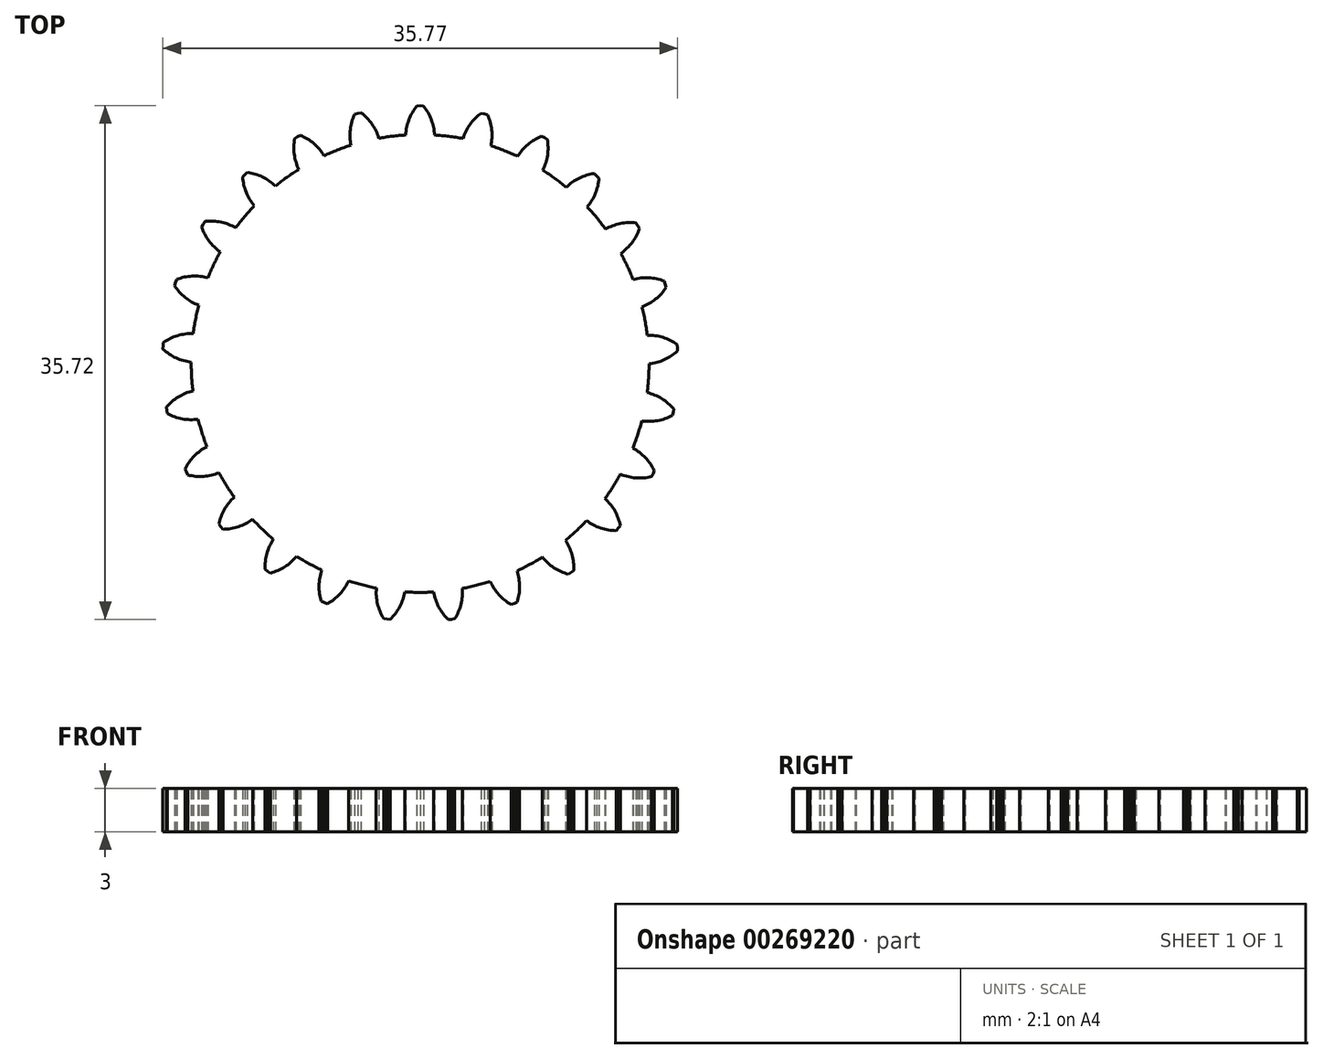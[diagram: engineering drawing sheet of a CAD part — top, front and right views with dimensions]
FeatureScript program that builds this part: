
annotation { "Feature Type Name" : "Feature", "Feature Type Description" : "" }
export const myFeature = defineFeature(function(context is Context, id is Id, definition is map)
    precondition{}
    {
        {
            var Q0;
            Q0=qCreatedBy(makeId("Top.planeOp"),FACE);
            var sketch = newSketch(context, id + "F0", { "sketchPlane" : qUnion([Q0])});
            skCircle(sketch, "E0", {"center": v(0, 0) * mm, "radius": 15.91 * mm});
            skCircle(sketch, "E1", {"center": v(0, 0) * mm, "radius": 16.91 * mm, "construction": true});
            skCircle(sketch, "E2", {"center": v(0, 0) * mm, "radius": 17.91 * mm, "construction": true});
            skLineSegment(sketch, "E3", {"start": v(0, 0) * mm, "end": v(0, 30.14) * mm, "construction": true});
            skLineSegment(sketch, "E4", {"start": v(0, 0) * mm, "end": v(-1.77, 28.18) * mm, "construction": true});
            skPoint(sketch, "E5", {"position": v(-1, 15.88) * mm});
            skPoint(sketch, "E6", {"position": v(0, 15.91) * mm});
            skLineSegment(sketch, "E7", {"start": v(-1, 15.88) * mm, "end": v(0, 15.91) * mm, "construction": true});
            skCircle(sketch, "E8", {"center": v(0, 16.91) * mm, "radius": 2.73 * mm, "construction": true});
            skLineSegment(sketch, "E9", {"start": v(0, 17.92) * mm, "end": v(0, 15.91) * mm});
            skArc(sketch, "E10", {"start": v(-0.23, 17.9) * mm, "mid": v(-0.78, 16.96) * mm, "end": v(-1, 15.88) * mm});
            skArc(sketch, "E11", {"start": v(-1, 15.88) * mm, "mid": v(5.7, 14.49) * mm, "end": v(-0.23, 17.9) * mm, "construction": true});
            skLineSegment(sketch, "E12", {"start": v(-0.23, 17.9) * mm, "end": v(0, 17.92) * mm});
            skLineSegment(sketch, "E13.MirrorCS", {"start": v(0.23, 17.9) * mm, "end": v(0, 17.92) * mm});
            skArc(sketch, "E14.MirrorCS", {"start": v(0.23, 17.9) * mm, "mid": v(0.78, 16.96) * mm, "end": v(1, 15.88) * mm});
            skLineSegment(sketch, "E15.1.0", {"start": v(4.46, 17.35) * mm, "end": v(3.96, 15.41) * mm});
            skPoint(sketch, "E15.1.1", {"position": v(3.96, 15.41) * mm});
            skArc(sketch, "E15.1.2", {"start": v(4.68, 17.28) * mm, "mid": v(4.97, 16.23) * mm, "end": v(4.92, 15.13) * mm});
            skPoint(sketch, "E15.1.3", {"position": v(2.99, 15.63) * mm});
            skLineSegment(sketch, "E15.1.4", {"start": v(2.99, 15.63) * mm, "end": v(3.96, 15.41) * mm, "construction": true});
            skArc(sketch, "E15.1.5", {"start": v(4.24, 17.4) * mm, "mid": v(3.47, 16.61) * mm, "end": v(2.99, 15.63) * mm});
            skLineSegment(sketch, "E15.1.6", {"start": v(4.68, 17.28) * mm, "end": v(4.46, 17.35) * mm});
            skLineSegment(sketch, "E15.1.7", {"start": v(4.24, 17.4) * mm, "end": v(4.46, 17.35) * mm});
            skLineSegment(sketch, "E15.2.0", {"start": v(8.64, 15.7) * mm, "end": v(7.67, 13.94) * mm});
            skPoint(sketch, "E15.2.1", {"position": v(7.67, 13.94) * mm});
            skArc(sketch, "E15.2.2", {"start": v(8.84, 15.58) * mm, "mid": v(8.86, 14.48) * mm, "end": v(8.53, 13.43) * mm});
            skPoint(sketch, "E15.2.3", {"position": v(6.78, 14.4) * mm});
            skLineSegment(sketch, "E15.2.4", {"start": v(6.78, 14.4) * mm, "end": v(7.67, 13.94) * mm, "construction": true});
            skArc(sketch, "E15.2.5", {"start": v(8.43, 15.8) * mm, "mid": v(7.5, 15.23) * mm, "end": v(6.78, 14.4) * mm});
            skLineSegment(sketch, "E15.2.6", {"start": v(8.84, 15.58) * mm, "end": v(8.64, 15.7) * mm});
            skLineSegment(sketch, "E15.2.7", {"start": v(8.43, 15.8) * mm, "end": v(8.64, 15.7) * mm});
            skLineSegment(sketch, "E15.3.0", {"start": v(12.28, 13.05) * mm, "end": v(10.9, 11.6) * mm});
            skPoint(sketch, "E15.3.1", {"position": v(10.9, 11.6) * mm});
            skArc(sketch, "E15.3.2", {"start": v(12.43, 12.88) * mm, "mid": v(12.18, 11.82) * mm, "end": v(11.61, 10.88) * mm});
            skPoint(sketch, "E15.3.3", {"position": v(10.15, 12.25) * mm});
            skLineSegment(sketch, "E15.3.4", {"start": v(10.15, 12.25) * mm, "end": v(10.9, 11.6) * mm, "construction": true});
            skArc(sketch, "E15.3.5", {"start": v(12.1, 13.2) * mm, "mid": v(11.05, 12.88) * mm, "end": v(10.15, 12.25) * mm});
            skLineSegment(sketch, "E15.3.6", {"start": v(12.43, 12.88) * mm, "end": v(12.28, 13.05) * mm});
            skLineSegment(sketch, "E15.3.7", {"start": v(12.1, 13.2) * mm, "end": v(12.28, 13.05) * mm});
            skLineSegment(sketch, "E15.4.0", {"start": v(15.14, 9.58) * mm, "end": v(13.45, 8.51) * mm});
            skPoint(sketch, "E15.4.1", {"position": v(13.45, 8.51) * mm});
            skArc(sketch, "E15.4.2", {"start": v(15.25, 9.38) * mm, "mid": v(14.74, 8.41) * mm, "end": v(13.95, 7.65) * mm});
            skPoint(sketch, "E15.4.3", {"position": v(12.88, 9.34) * mm});
            skLineSegment(sketch, "E15.4.4", {"start": v(12.88, 9.34) * mm, "end": v(13.45, 8.51) * mm, "construction": true});
            skArc(sketch, "E15.4.5", {"start": v(15, 9.77) * mm, "mid": v(13.91, 9.72) * mm, "end": v(12.88, 9.34) * mm});
            skLineSegment(sketch, "E15.4.6", {"start": v(15.25, 9.38) * mm, "end": v(15.14, 9.58) * mm});
            skLineSegment(sketch, "E15.4.7", {"start": v(15, 9.77) * mm, "end": v(15.14, 9.58) * mm});
            skLineSegment(sketch, "E15.5.0", {"start": v(17.05, 5.51) * mm, "end": v(15.14, 4.9) * mm});
            skPoint(sketch, "E15.5.1", {"position": v(15.14, 4.9) * mm});
            skArc(sketch, "E15.5.2", {"start": v(17.1, 5.3) * mm, "mid": v(16.37, 4.48) * mm, "end": v(15.42, 3.93) * mm});
            skPoint(sketch, "E15.5.3", {"position": v(14.8, 5.84) * mm});
            skLineSegment(sketch, "E15.5.4", {"start": v(14.8, 5.84) * mm, "end": v(15.14, 4.9) * mm, "construction": true});
            skArc(sketch, "E15.5.5", {"start": v(16.97, 5.73) * mm, "mid": v(15.9, 5.95) * mm, "end": v(14.8, 5.84) * mm});
            skLineSegment(sketch, "E15.5.6", {"start": v(17.1, 5.3) * mm, "end": v(17.05, 5.51) * mm});
            skLineSegment(sketch, "E15.5.7", {"start": v(16.97, 5.73) * mm, "end": v(17.05, 5.51) * mm});
            skLineSegment(sketch, "E15.6.0", {"start": v(17.88, 1.1) * mm, "end": v(15.88, 0.97) * mm});
            skPoint(sketch, "E15.6.1", {"position": v(15.88, 0.97) * mm});
            skArc(sketch, "E15.6.2", {"start": v(17.89, 0.86) * mm, "mid": v(16.97, 0.26) * mm, "end": v(15.91, -0.03) * mm});
            skPoint(sketch, "E15.6.3", {"position": v(15.8, 1.97) * mm});
            skLineSegment(sketch, "E15.6.4", {"start": v(15.8, 1.97) * mm, "end": v(15.88, 0.97) * mm, "construction": true});
            skArc(sketch, "E15.6.5", {"start": v(17.86, 1.32) * mm, "mid": v(16.88, 1.8) * mm, "end": v(15.8, 1.97) * mm});
            skLineSegment(sketch, "E15.6.6", {"start": v(17.89, 0.86) * mm, "end": v(17.88, 1.1) * mm});
            skLineSegment(sketch, "E15.6.7", {"start": v(17.86, 1.32) * mm, "end": v(17.88, 1.1) * mm});
            skLineSegment(sketch, "E15.7.0", {"start": v(17.6, -3.4) * mm, "end": v(15.63, -3.01) * mm});
            skPoint(sketch, "E15.7.1", {"position": v(15.63, -3.01) * mm});
            skArc(sketch, "E15.7.2", {"start": v(17.54, -3.62) * mm, "mid": v(16.5, -3.97) * mm, "end": v(15.4, -3.99) * mm});
            skPoint(sketch, "E15.7.3", {"position": v(15.78, -2.03) * mm});
            skLineSegment(sketch, "E15.7.4", {"start": v(15.78, -2.03) * mm, "end": v(15.63, -3.01) * mm, "construction": true});
            skArc(sketch, "E15.7.5", {"start": v(17.62, -3.17) * mm, "mid": v(16.8, -2.45) * mm, "end": v(15.78, -2.03) * mm});
            skLineSegment(sketch, "E15.7.6", {"start": v(17.54, -3.62) * mm, "end": v(17.6, -3.4) * mm});
            skLineSegment(sketch, "E15.7.7", {"start": v(17.62, -3.17) * mm, "end": v(17.6, -3.4) * mm});
            skLineSegment(sketch, "E15.8.0", {"start": v(16.2, -7.67) * mm, "end": v(14.38, -6.8) * mm});
            skPoint(sketch, "E15.8.1", {"position": v(14.38, -6.8) * mm});
            skArc(sketch, "E15.8.2", {"start": v(16.09, -7.87) * mm, "mid": v(15, -7.96) * mm, "end": v(13.93, -7.7) * mm});
            skPoint(sketch, "E15.8.3", {"position": v(14.78, -5.9) * mm});
            skLineSegment(sketch, "E15.8.4", {"start": v(14.78, -5.9) * mm, "end": v(14.38, -6.8) * mm, "construction": true});
            skArc(sketch, "E15.8.5", {"start": v(16.28, -7.45) * mm, "mid": v(15.66, -6.55) * mm, "end": v(14.78, -5.9) * mm});
            skLineSegment(sketch, "E15.8.6", {"start": v(16.09, -7.87) * mm, "end": v(16.2, -7.67) * mm});
            skLineSegment(sketch, "E15.8.7", {"start": v(16.28, -7.45) * mm, "end": v(16.2, -7.67) * mm});
            skLineSegment(sketch, "E15.9.0", {"start": v(13.77, -11.46) * mm, "end": v(12.23, -10.18) * mm});
            skPoint(sketch, "E15.9.1", {"position": v(12.23, -10.18) * mm});
            skArc(sketch, "E15.9.2", {"start": v(13.62, -11.63) * mm, "mid": v(12.54, -11.44) * mm, "end": v(11.57, -10.92) * mm});
            skPoint(sketch, "E15.9.3", {"position": v(12.85, -9.39) * mm});
            skLineSegment(sketch, "E15.9.4", {"start": v(12.85, -9.39) * mm, "end": v(12.23, -10.18) * mm, "construction": true});
            skArc(sketch, "E15.9.5", {"start": v(13.91, -11.27) * mm, "mid": v(13.53, -10.25) * mm, "end": v(12.85, -9.39) * mm});
            skLineSegment(sketch, "E15.9.6", {"start": v(13.62, -11.63) * mm, "end": v(13.77, -11.46) * mm});
            skLineSegment(sketch, "E15.9.7", {"start": v(13.91, -11.27) * mm, "end": v(13.77, -11.46) * mm});
            skLineSegment(sketch, "E15.10.0", {"start": v(10.49, -14.52) * mm, "end": v(9.32, -12.9) * mm});
            skPoint(sketch, "E15.10.1", {"position": v(9.32, -12.9) * mm});
            skArc(sketch, "E15.10.2", {"start": v(10.3, -14.65) * mm, "mid": v(9.3, -14.2) * mm, "end": v(8.49, -13.46) * mm});
            skPoint(sketch, "E15.10.3", {"position": v(10.1, -12.3) * mm});
            skLineSegment(sketch, "E15.10.4", {"start": v(10.1, -12.3) * mm, "end": v(9.32, -12.9) * mm, "construction": true});
            skArc(sketch, "E15.10.5", {"start": v(10.67, -14.38) * mm, "mid": v(10.56, -13.3) * mm, "end": v(10.1, -12.3) * mm});
            skLineSegment(sketch, "E15.10.6", {"start": v(10.3, -14.65) * mm, "end": v(10.49, -14.52) * mm});
            skLineSegment(sketch, "E15.10.7", {"start": v(10.67, -14.38) * mm, "end": v(10.49, -14.52) * mm});
            skLineSegment(sketch, "E15.11.0", {"start": v(6.54, -16.68) * mm, "end": v(5.81, -14.81) * mm});
            skPoint(sketch, "E15.11.1", {"position": v(5.81, -14.81) * mm});
            skArc(sketch, "E15.11.2", {"start": v(6.33, -16.75) * mm, "mid": v(5.47, -16.07) * mm, "end": v(4.87, -15.15) * mm});
            skPoint(sketch, "E15.11.3", {"position": v(6.73, -14.42) * mm});
            skLineSegment(sketch, "E15.11.4", {"start": v(6.73, -14.42) * mm, "end": v(5.81, -14.81) * mm, "construction": true});
            skArc(sketch, "E15.11.5", {"start": v(6.75, -16.59) * mm, "mid": v(6.91, -15.5) * mm, "end": v(6.73, -14.42) * mm});
            skLineSegment(sketch, "E15.11.6", {"start": v(6.33, -16.75) * mm, "end": v(6.54, -16.68) * mm});
            skLineSegment(sketch, "E15.11.7", {"start": v(6.75, -16.59) * mm, "end": v(6.54, -16.68) * mm});
            skLineSegment(sketch, "E15.12.0", {"start": v(2.18, -17.78) * mm, "end": v(1.94, -15.8) * mm});
            skPoint(sketch, "E15.12.1", {"position": v(1.94, -15.8) * mm});
            skArc(sketch, "E15.12.2", {"start": v(1.96, -17.8) * mm, "mid": v(1.3, -16.92) * mm, "end": v(0.94, -15.89) * mm});
            skPoint(sketch, "E15.12.3", {"position": v(2.93, -15.64) * mm});
            skLineSegment(sketch, "E15.12.4", {"start": v(2.93, -15.64) * mm, "end": v(1.94, -15.8) * mm, "construction": true});
            skArc(sketch, "E15.12.5", {"start": v(2.4, -17.74) * mm, "mid": v(2.84, -16.73) * mm, "end": v(2.93, -15.64) * mm});
            skLineSegment(sketch, "E15.12.6", {"start": v(1.96, -17.8) * mm, "end": v(2.18, -17.78) * mm});
            skLineSegment(sketch, "E15.12.7", {"start": v(2.4, -17.74) * mm, "end": v(2.18, -17.78) * mm});
            skLineSegment(sketch, "E15.13.0", {"start": v(-2.31, -17.77) * mm, "end": v(-2.05, -15.78) * mm});
            skPoint(sketch, "E15.13.1", {"position": v(-2.05, -15.78) * mm});
            skArc(sketch, "E15.13.2", {"start": v(-2.54, -17.73) * mm, "mid": v(-2.96, -16.71) * mm, "end": v(-3.04, -15.62) * mm});
            skPoint(sketch, "E15.13.3", {"position": v(-1.06, -15.88) * mm});
            skLineSegment(sketch, "E15.13.4", {"start": v(-1.06, -15.88) * mm, "end": v(-2.05, -15.78) * mm, "construction": true});
            skArc(sketch, "E15.13.5", {"start": v(-2.08, -17.78) * mm, "mid": v(-1.42, -16.91) * mm, "end": v(-1.06, -15.88) * mm});
            skLineSegment(sketch, "E15.13.6", {"start": v(-2.54, -17.73) * mm, "end": v(-2.31, -17.77) * mm});
            skLineSegment(sketch, "E15.13.7", {"start": v(-2.08, -17.78) * mm, "end": v(-2.31, -17.77) * mm});
            skLineSegment(sketch, "E15.14.0", {"start": v(-6.66, -16.63) * mm, "end": v(-5.92, -14.77) * mm});
            skPoint(sketch, "E15.14.1", {"position": v(-5.92, -14.77) * mm});
            skArc(sketch, "E15.14.2", {"start": v(-6.87, -16.54) * mm, "mid": v(-7.03, -15.45) * mm, "end": v(-6.83, -14.37) * mm});
            skPoint(sketch, "E15.14.3", {"position": v(-4.98, -15.11) * mm});
            skLineSegment(sketch, "E15.14.4", {"start": v(-4.98, -15.11) * mm, "end": v(-5.92, -14.77) * mm, "construction": true});
            skArc(sketch, "E15.14.5", {"start": v(-6.45, -16.7) * mm, "mid": v(-5.59, -16.03) * mm, "end": v(-4.98, -15.11) * mm});
            skLineSegment(sketch, "E15.14.6", {"start": v(-6.87, -16.54) * mm, "end": v(-6.66, -16.63) * mm});
            skLineSegment(sketch, "E15.14.7", {"start": v(-6.45, -16.7) * mm, "end": v(-6.66, -16.63) * mm});
            skLineSegment(sketch, "E15.15.0", {"start": v(-10.6, -14.45) * mm, "end": v(-9.4, -12.83) * mm});
            skPoint(sketch, "E15.15.1", {"position": v(-9.4, -12.83) * mm});
            skArc(sketch, "E15.15.2", {"start": v(-10.77, -14.3) * mm, "mid": v(-10.65, -13.21) * mm, "end": v(-10.2, -12.22) * mm});
            skPoint(sketch, "E15.15.3", {"position": v(-8.59, -13.4) * mm});
            skLineSegment(sketch, "E15.15.4", {"start": v(-8.59, -13.4) * mm, "end": v(-9.4, -12.83) * mm, "construction": true});
            skArc(sketch, "E15.15.5", {"start": v(-10.4, -14.57) * mm, "mid": v(-9.4, -14.13) * mm, "end": v(-8.59, -13.4) * mm});
            skLineSegment(sketch, "E15.15.6", {"start": v(-10.77, -14.3) * mm, "end": v(-10.6, -14.45) * mm});
            skLineSegment(sketch, "E15.15.7", {"start": v(-10.4, -14.57) * mm, "end": v(-10.6, -14.45) * mm});
            skLineSegment(sketch, "E15.16.0", {"start": v(-13.86, -11.36) * mm, "end": v(-12.3, -10.09) * mm});
            skPoint(sketch, "E15.16.1", {"position": v(-12.3, -10.09) * mm});
            skArc(sketch, "E15.16.2", {"start": v(-14, -11.17) * mm, "mid": v(-13.6, -10.15) * mm, "end": v(-12.92, -9.3) * mm});
            skPoint(sketch, "E15.16.3", {"position": v(-11.65, -10.84) * mm});
            skLineSegment(sketch, "E15.16.4", {"start": v(-11.65, -10.84) * mm, "end": v(-12.3, -10.09) * mm, "construction": true});
            skArc(sketch, "E15.16.5", {"start": v(-13.7, -11.53) * mm, "mid": v(-12.62, -11.35) * mm, "end": v(-11.65, -10.84) * mm});
            skLineSegment(sketch, "E15.16.6", {"start": v(-14, -11.17) * mm, "end": v(-13.86, -11.36) * mm});
            skLineSegment(sketch, "E15.16.7", {"start": v(-13.7, -11.53) * mm, "end": v(-13.86, -11.36) * mm});
            skLineSegment(sketch, "E15.17.0", {"start": v(-16.25, -7.55) * mm, "end": v(-14.43, -6.7) * mm});
            skPoint(sketch, "E15.17.1", {"position": v(-14.43, -6.7) * mm});
            skArc(sketch, "E15.17.2", {"start": v(-16.33, -7.34) * mm, "mid": v(-15.7, -6.44) * mm, "end": v(-14.82, -5.78) * mm});
            skPoint(sketch, "E15.17.3", {"position": v(-13.98, -7.6) * mm});
            skLineSegment(sketch, "E15.17.4", {"start": v(-13.98, -7.6) * mm, "end": v(-14.43, -6.7) * mm, "construction": true});
            skArc(sketch, "E15.17.5", {"start": v(-16.14, -7.75) * mm, "mid": v(-15.05, -7.85) * mm, "end": v(-13.98, -7.6) * mm});
            skLineSegment(sketch, "E15.17.6", {"start": v(-16.33, -7.34) * mm, "end": v(-16.25, -7.55) * mm});
            skLineSegment(sketch, "E15.17.7", {"start": v(-16.14, -7.75) * mm, "end": v(-16.25, -7.55) * mm});
            skLineSegment(sketch, "E15.18.0", {"start": v(-17.62, -3.26) * mm, "end": v(-15.65, -2.9) * mm});
            skPoint(sketch, "E15.18.1", {"position": v(-15.65, -2.9) * mm});
            skArc(sketch, "E15.18.2", {"start": v(-17.65, -3.04) * mm, "mid": v(-16.81, -2.33) * mm, "end": v(-15.8, -1.91) * mm});
            skPoint(sketch, "E15.18.3", {"position": v(-15.43, -3.88) * mm});
            skLineSegment(sketch, "E15.18.4", {"start": v(-15.43, -3.88) * mm, "end": v(-15.65, -2.9) * mm, "construction": true});
            skArc(sketch, "E15.18.5", {"start": v(-17.56, -3.49) * mm, "mid": v(-16.53, -3.85) * mm, "end": v(-15.43, -3.88) * mm});
            skLineSegment(sketch, "E15.18.6", {"start": v(-17.65, -3.04) * mm, "end": v(-17.62, -3.26) * mm});
            skLineSegment(sketch, "E15.18.7", {"start": v(-17.56, -3.49) * mm, "end": v(-17.62, -3.26) * mm});
            skLineSegment(sketch, "E15.19.0", {"start": v(-17.87, 1.22) * mm, "end": v(-15.88, 1.09) * mm});
            skPoint(sketch, "E15.19.1", {"position": v(-15.88, 1.09) * mm});
            skArc(sketch, "E15.19.2", {"start": v(-17.85, 1.45) * mm, "mid": v(-16.86, 1.93) * mm, "end": v(-15.78, 2.08) * mm});
            skPoint(sketch, "E15.19.3", {"position": v(-15.91, 0.09) * mm});
            skLineSegment(sketch, "E15.19.4", {"start": v(-15.91, 0.09) * mm, "end": v(-15.88, 1.09) * mm, "construction": true});
            skArc(sketch, "E15.19.5", {"start": v(-17.88, 1) * mm, "mid": v(-16.97, 0.38) * mm, "end": v(-15.91, 0.09) * mm});
            skLineSegment(sketch, "E15.19.6", {"start": v(-17.85, 1.45) * mm, "end": v(-17.87, 1.22) * mm});
            skLineSegment(sketch, "E15.19.7", {"start": v(-17.88, 1) * mm, "end": v(-17.87, 1.22) * mm});
            skLineSegment(sketch, "E15.20.0", {"start": v(-17, 5.64) * mm, "end": v(-15.1, 5) * mm});
            skPoint(sketch, "E15.20.1", {"position": v(-15.1, 5) * mm});
            skArc(sketch, "E15.20.2", {"start": v(-16.92, 5.85) * mm, "mid": v(-15.85, 6.07) * mm, "end": v(-14.76, 5.94) * mm});
            skPoint(sketch, "E15.20.3", {"position": v(-15.4, 4.05) * mm});
            skLineSegment(sketch, "E15.20.4", {"start": v(-15.4, 4.05) * mm, "end": v(-15.1, 5) * mm, "construction": true});
            skArc(sketch, "E15.20.5", {"start": v(-17.07, 5.41) * mm, "mid": v(-16.34, 4.6) * mm, "end": v(-15.4, 4.05) * mm});
            skLineSegment(sketch, "E15.20.6", {"start": v(-16.92, 5.85) * mm, "end": v(-17, 5.64) * mm});
            skLineSegment(sketch, "E15.20.7", {"start": v(-17.07, 5.41) * mm, "end": v(-17, 5.64) * mm});
            skLineSegment(sketch, "E15.21.0", {"start": v(-15.07, 9.7) * mm, "end": v(-13.38, 8.6) * mm});
            skPoint(sketch, "E15.21.1", {"position": v(-13.38, 8.6) * mm});
            skArc(sketch, "E15.21.2", {"start": v(-14.94, 9.88) * mm, "mid": v(-13.84, 9.83) * mm, "end": v(-12.82, 9.43) * mm});
            skPoint(sketch, "E15.21.3", {"position": v(-13.9, 7.75) * mm});
            skLineSegment(sketch, "E15.21.4", {"start": v(-13.9, 7.75) * mm, "end": v(-13.38, 8.6) * mm, "construction": true});
            skArc(sketch, "E15.21.5", {"start": v(-15.18, 9.5) * mm, "mid": v(-14.68, 8.52) * mm, "end": v(-13.9, 7.75) * mm});
            skLineSegment(sketch, "E15.21.6", {"start": v(-14.94, 9.88) * mm, "end": v(-15.07, 9.7) * mm});
            skLineSegment(sketch, "E15.21.7", {"start": v(-15.18, 9.5) * mm, "end": v(-15.07, 9.7) * mm});
            skLineSegment(sketch, "E15.22.0", {"start": v(-12.18, 13.14) * mm, "end": v(-10.82, 11.67) * mm});
            skPoint(sketch, "E15.22.1", {"position": v(-10.82, 11.67) * mm});
            skArc(sketch, "E15.22.2", {"start": v(-12, 13.29) * mm, "mid": v(-10.96, 12.96) * mm, "end": v(-10.06, 12.33) * mm});
            skPoint(sketch, "E15.22.3", {"position": v(-11.53, 10.97) * mm});
            skLineSegment(sketch, "E15.22.4", {"start": v(-11.53, 10.97) * mm, "end": v(-10.82, 11.67) * mm, "construction": true});
            skArc(sketch, "E15.22.5", {"start": v(-12.34, 12.97) * mm, "mid": v(-12.1, 11.9) * mm, "end": v(-11.53, 10.97) * mm});
            skLineSegment(sketch, "E15.22.6", {"start": v(-12, 13.29) * mm, "end": v(-12.18, 13.14) * mm});
            skLineSegment(sketch, "E15.22.7", {"start": v(-12.34, 12.97) * mm, "end": v(-12.18, 13.14) * mm});
            skLineSegment(sketch, "E15.23.0", {"start": v(-8.53, 15.76) * mm, "end": v(-7.57, 14) * mm});
            skPoint(sketch, "E15.23.1", {"position": v(-7.57, 14) * mm});
            skArc(sketch, "E15.23.2", {"start": v(-8.32, 15.86) * mm, "mid": v(-7.39, 15.28) * mm, "end": v(-6.68, 14.44) * mm});
            skPoint(sketch, "E15.23.3", {"position": v(-8.44, 13.5) * mm});
            skLineSegment(sketch, "E15.23.4", {"start": v(-8.44, 13.5) * mm, "end": v(-7.57, 14) * mm, "construction": true});
            skArc(sketch, "E15.23.5", {"start": v(-8.72, 15.64) * mm, "mid": v(-8.75, 14.54) * mm, "end": v(-8.44, 13.5) * mm});
            skLineSegment(sketch, "E15.23.6", {"start": v(-8.32, 15.86) * mm, "end": v(-8.53, 15.76) * mm});
            skLineSegment(sketch, "E15.23.7", {"start": v(-8.72, 15.64) * mm, "end": v(-8.53, 15.76) * mm});
            skLineSegment(sketch, "E15.24.0", {"start": v(-4.33, 17.38) * mm, "end": v(-3.85, 15.44) * mm});
            skPoint(sketch, "E15.24.1", {"position": v(-3.85, 15.44) * mm});
            skArc(sketch, "E15.24.2", {"start": v(-4.1, 17.43) * mm, "mid": v(-3.35, 16.64) * mm, "end": v(-2.87, 15.65) * mm});
            skPoint(sketch, "E15.24.3", {"position": v(-4.81, 15.17) * mm});
            skLineSegment(sketch, "E15.24.4", {"start": v(-4.81, 15.17) * mm, "end": v(-3.85, 15.44) * mm, "construction": true});
            skArc(sketch, "E15.24.5", {"start": v(-4.55, 17.32) * mm, "mid": v(-4.86, 16.26) * mm, "end": v(-4.81, 15.17) * mm});
            skLineSegment(sketch, "E15.24.6", {"start": v(-4.1, 17.43) * mm, "end": v(-4.33, 17.38) * mm});
            skLineSegment(sketch, "E15.24.7", {"start": v(-4.55, 17.32) * mm, "end": v(-4.33, 17.38) * mm});
            skLineSegment(sketch, "E15.anchor1", {"start": v(0, 0) * mm, "end": v(-2.46, 15.72) * mm, "construction": true});
            skLineSegment(sketch, "E15.anchor2", {"start": v(0, 0) * mm, "end": v(-6.2, 14.66) * mm, "construction": true});
            skSolve(sketch);
        }
        {
            var Q0;
            Q0 = qSketchRegion(id + "F0", true);
            extrude(context, id + "F1", {"entities" : qUnion([Q0]), "depth" : 3 * mm});
        }
    });
